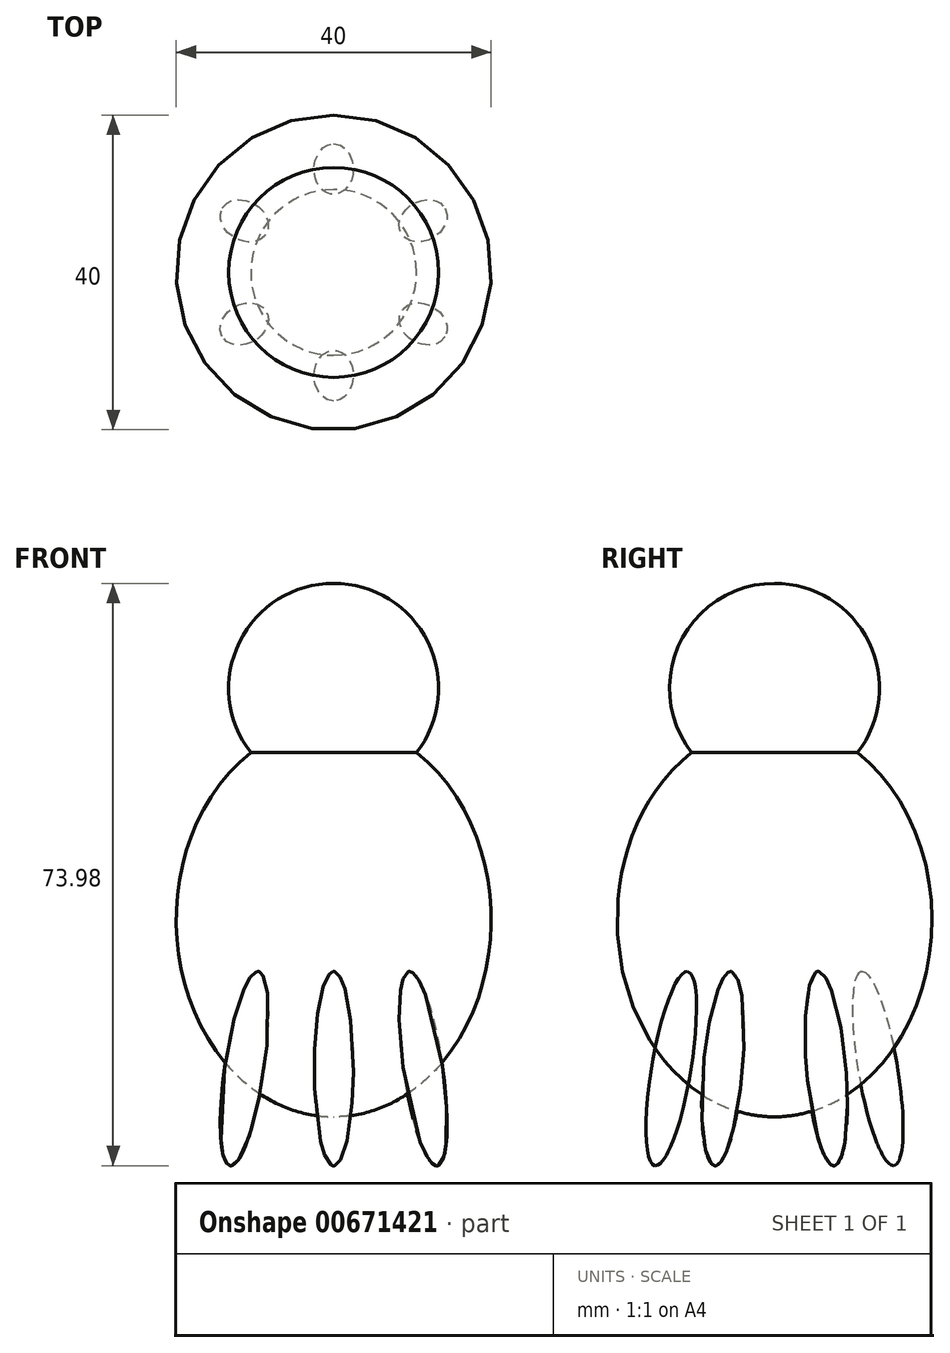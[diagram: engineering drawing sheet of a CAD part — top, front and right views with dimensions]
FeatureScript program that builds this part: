
annotation { "Feature Type Name" : "Feature", "Feature Type Description" : "" }
export const myFeature = defineFeature(function(context is Context, id is Id, definition is map)
    precondition{}
    {
        {
            assignVariable(context, id + "F0", {"name" : "legs", "anyValue" : 6});
        }
        {
            assignVariable(context, id + "F1", {"name" : "eyesW", "anyValue" : 100});
        }
        {
            var Q0;
            Q0=qCreatedBy(makeId("Right.planeOp"),FACE);
            var sketch = newSketch(context, id + "F2", { "sketchPlane" : qUnion([Q0])});
            skEllipse(sketch, "E0", {"center": v(0, 35) * mm, "majorRadius": 25 * mm, "minorRadius": 20 * mm, "majorAxis": v(0, 1)});
            skEllipse(sketch, "E1", {"center": v(-13.11, 16.13) * mm, "majorRadius": 12.5 * mm, "minorRadius": 2.5 * mm, "majorAxis": v(0.17, 0.99)});
            skLineSegment(sketch, "E2", {"start": v(0, 60) * mm, "end": v(0, 10) * mm});
            skLineSegment(sketch, "E3", {"start": v(-11.04, 28.46) * mm, "end": v(-15.19, 3.8) * mm});
            skLineSegment(sketch, "E4", {"start": v(-0.25, 60) * mm, "end": v(0.25, 60) * mm});
            skPoint(sketch, "E5.third.point", {"position": v(0, 91.67) * mm});
            skPoint(sketch, "E5.third.point.positionSnap0", {"position": v(0, 60) * mm});
            skLineSegment(sketch, "E6", {"start": v(0, 51.12) * mm, "end": v(0, 91.67) * mm});
            skCircle(sketch, "E7", {"center": v(0, 64.45) * mm, "radius": 13.33 * mm});
            skCircle(sketch, "E8", {"center": v(-13.24, 66) * mm, "radius": 3.5 * mm});
            skLineSegment(sketch, "E9", {"start": v(-9.74, 66) * mm, "end": v(-16.74, 66) * mm});
            skSolve(sketch);
        }
        {
            var Q0;
            {var subQ0=sQuery(id+"F2.wireOp",EDGE,"E2");Q0=makeQuery(id+"F2.imprint","IMPRINT",FACE,{"disambiguationData":[TD([[makeQuery(id+"F2.imprint","IMPRINT",EDGE,{"derivedFrom":subQ0}),1.0]])]});}
            var Q1;
            Q1=sQuery(id+"F2.wireOp",EDGE,"E2");
            revolve(context, id + "F3", {"entities" : qUnion([Q0]), "axis" : qUnion([Q1]), "revolveType" : RevolveType.FULL});
        }
        {
            var Q0;
            {var subQ0=sQuery(id+"F2.wireOp",EDGE,"E1");var subQ1=sQuery(id+"F2.wireOp",EDGE,"E0");var subQ2=makeQuery(id+"F2.imprint","INTERSECT",VERTEX,{"disambiguationData":[OD(0.0)],"derivedFrom":[subQ1,subQ0]});Q0=makeQuery(id+"F2.imprint","IMPRINT",FACE,{"disambiguationData":[TD([[makeQuery(id+"F2.imprint","IMPRINT",EDGE,{"disambiguationData":[TD([[subQ2,-1.0]])],"derivedFrom":subQ1}),1.0]])]});}
            var Q1;
            {var subQ0=sQuery(id+"F2.wireOp",EDGE,"E1");var subQ1=sQuery(id+"F2.wireOp",EDGE,"E0");var subQ2=makeQuery(id+"F2.imprint","INTERSECT",VERTEX,{"disambiguationData":[OD(0.0)],"derivedFrom":[subQ1,subQ0]});Q1=makeQuery(id+"F2.imprint","IMPRINT",FACE,{"disambiguationData":[TD([[makeQuery(id+"F2.imprint","IMPRINT",EDGE,{"disambiguationData":[TD([[subQ2,-1.0]])],"derivedFrom":subQ1}),-1.0]])]});}
            var Q2;
            Q2=sQuery(id+"F2.wireOp",EDGE,"E3");
            revolve(context, id + "F4", {"entities" : qUnion([Q0, Q1]), "axis" : qUnion([Q2]), "revolveType" : RevolveType.FULL});
        }
        {
            var Q0;
            Q0=makeQuery(id+"F4.opRevolve","SWEPT_BODY",BODY,{"disambiguationData":[OSD([sQuery(id+"F2.wireOp",EDGE,"E1"),sQuery(id+"F2.wireOp",EDGE,"E3")])]});
            var Q1;
            Q1=sQuery(id+"F2.wireOp",EDGE,"E2");
            circularPattern(context, id + "F5", {"entities" : qUnion([Q0]), "axis" : qUnion([Q1]), "angle" : 360 * degree, "instanceCount" : getVariable(context, 'legs'), "equalSpace" : true});
        }
        {
            var Q0;
            {var subQ0=sQuery(id+"F2.wireOp",EDGE,"E0");var subQ1=makeQuery(id+"F2.imprint","INTERSECT",VERTEX,{"disambiguationData":[OD(1.0)],"derivedFrom":[subQ0,sQuery(id+"F2.wireOp",EDGE,"E4")]});Q0=makeQuery(id+"F2.imprint","IMPRINT",FACE,{"disambiguationData":[TD([[makeQuery(id+"F2.imprint","IMPRINT",EDGE,{"disambiguationData":[TD([[subQ1,1.0]])],"derivedFrom":subQ0}),-1.0]])]});}
            var Q1;
            {var subQ0=sQuery(id+"F2.wireOp",EDGE,"E4");var subQ1=sQuery(id+"F2.wireOp",EDGE,"E0");var subQ2=makeQuery(id+"F2.imprint","INTERSECT",VERTEX,{"disambiguationData":[OD(1.0)],"derivedFrom":[subQ1,subQ0]});Q1=makeQuery(id+"F2.imprint","IMPRINT",FACE,{"disambiguationData":[TD([[makeQuery(id+"F2.imprint","IMPRINT",EDGE,{"disambiguationData":[TD([[subQ2,1.0]])],"derivedFrom":subQ1}),1.0]])]});}
            var Q2;
            Q2=sQuery(id+"F2.wireOp",EDGE,"E2");
            revolve(context, id + "F6", {"operationType" : NewBodyOperationType.ADD, "surfaceOperationType" : NewSurfaceOperationType.NEW, "entities" : qUnion([Q0, Q1]), "axis" : qUnion([Q2]), "revolveType" : RevolveType.FULL});
        }
        {
            var Q0;
            {var subQ0=sQuery(id+"F2.wireOp",EDGE,"E8");var subQ1=sQuery(id+"F2.wireOp",EDGE,"E7");var subQ2=makeQuery(id+"F2.imprint","INTERSECT",VERTEX,{"disambiguationData":[OD(0.0)],"derivedFrom":[subQ1,subQ0]});Q0=makeQuery(id+"F2.imprint","IMPRINT",FACE,{"disambiguationData":[TD([[makeQuery(id+"F2.imprint","IMPRINT",EDGE,{"disambiguationData":[TD([[subQ2,-1.0]])],"derivedFrom":subQ1}),1.0]])]});}
            var Q1;
            {var subQ0=sQuery(id+"F2.wireOp",EDGE,"E8");var subQ1=sQuery(id+"F2.wireOp",EDGE,"E7");var subQ2=makeQuery(id+"F2.imprint","INTERSECT",VERTEX,{"disambiguationData":[OD(0.0)],"derivedFrom":[subQ1,subQ0]});Q1=makeQuery(id+"F2.imprint","IMPRINT",FACE,{"disambiguationData":[TD([[makeQuery(id+"F2.imprint","IMPRINT",EDGE,{"disambiguationData":[TD([[subQ2,-1.0]])],"derivedFrom":subQ1}),-1.0]])]});}
            var Q2;
            Q2=sQuery(id+"F2.wireOp",EDGE,"E9");
            revolve(context, id + "F7", {"surfaceOperationType" : NewSurfaceOperationType.NEW, "entities" : qUnion([Q0, Q1]), "axis" : qUnion([Q2]), "revolveType" : RevolveType.FULL, "oppositeDirection" : true});
        }
        {
            var Q0;
            Q0=makeQuery(id+"F7.opRevolve","SWEPT_BODY",BODY,{"disambiguationData":[OSD([sQuery(id+"F2.wireOp",EDGE,"E8"),sQuery(id+"F2.wireOp",EDGE,"E9")])]});
            var Q1;
            Q1=sQuery(id+"F2.wireOp",EDGE,"E2");
            circularPattern(context, id + "F8", {"entities" : qUnion([Q0]), "axis" : qUnion([Q1]), "angle" : (getVariable(context, 'eyesW')) * degree, "instanceCount" : 2, "equalSpace" : true});
        }
        {
            var Q0;
            Q0=makeQuery(id+"F7.opRevolve","SWEPT_BODY",BODY,{"disambiguationData":[OSD([sQuery(id+"F2.wireOp",EDGE,"E8"),sQuery(id+"F2.wireOp",EDGE,"E9")])]});
            var Q1;
            Q1=makeQuery(id+"F8.opPattern","COPY",BODY,{"derivedFrom":makeQuery(id+"F7.opRevolve","SWEPT_BODY",BODY,{"disambiguationData":[OSD([sQuery(id+"F2.wireOp",EDGE,"E8"),sQuery(id+"F2.wireOp",EDGE,"E9")])]}),"instanceName":"1"});
            var Q2;
            Q2=makeQuery(id+"F4.opRevolve","SWEPT_BODY",BODY,{"disambiguationData":[OSD([sQuery(id+"F2.wireOp",EDGE,"E1"),sQuery(id+"F2.wireOp",EDGE,"E3")])]});
            booleanBodies(context, id + "F9", {"operationType" : BooleanOperationType.SUBTRACTION, "tools" : qUnion([Q0, Q1]), "targets" : qUnion([Q2])});
        }
    });
